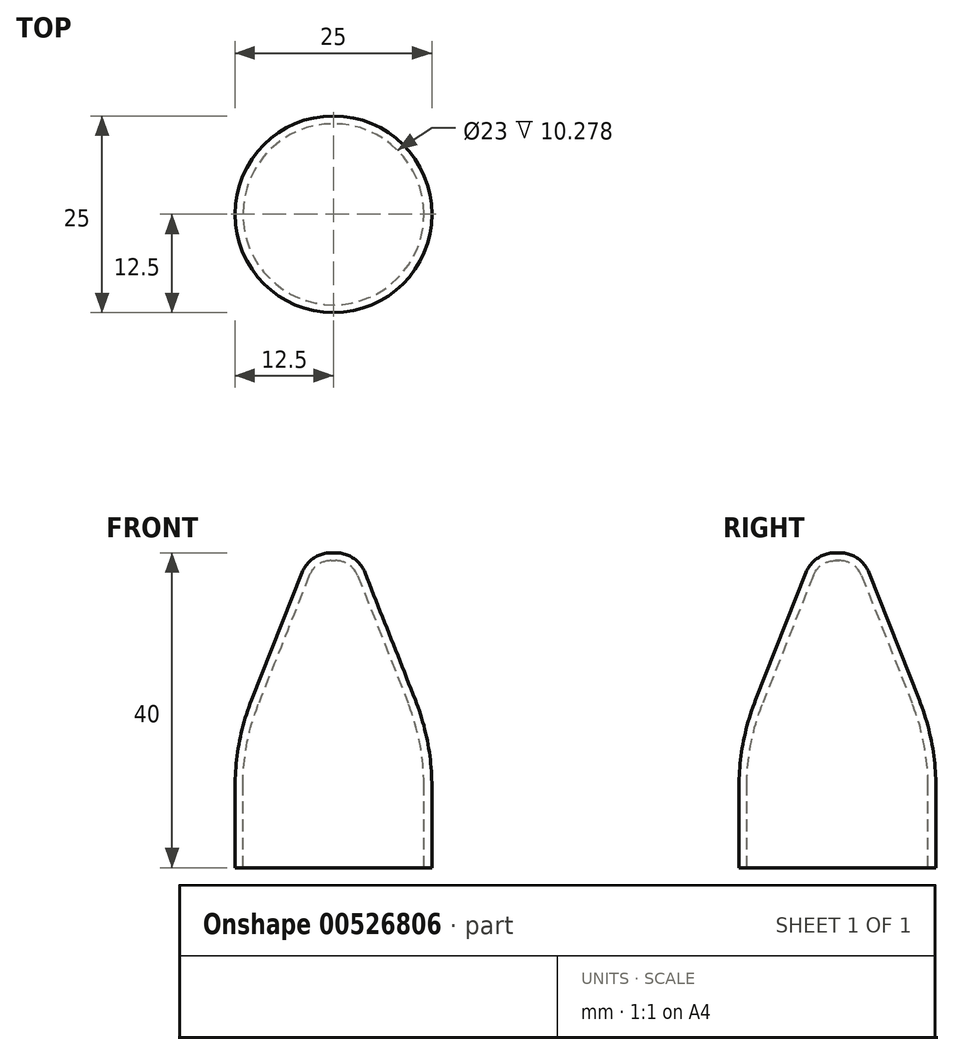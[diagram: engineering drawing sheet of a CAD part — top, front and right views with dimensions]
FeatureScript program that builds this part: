
annotation { "Feature Type Name" : "Feature", "Feature Type Description" : "" }
export const myFeature = defineFeature(function(context is Context, id is Id, definition is map)
    precondition{}
    {
        {
            var Q0;
            Q0=qCreatedBy(makeId("Front.planeOp"),FACE);
            var sketch = newSketch(context, id + "F0", { "sketchPlane" : qUnion([Q0])});
            skLineSegment(sketch, "E0.bottom", {"start": v(0, 0) * mm, "end": v(-12.5, 0) * mm});
            skLineSegment(sketch, "E0.right", {"start": v(-12.5, 0) * mm, "end": v(-12.5, 16) * mm});
            skLineSegment(sketch, "E1", {"start": v(-12.5, 16) * mm, "end": v(-3, 40) * mm});
            skLineSegment(sketch, "E2", {"start": v(-3, 40) * mm, "end": v(0, 40) * mm});
            skLineSegment(sketch, "E3", {"start": v(0, 40) * mm, "end": v(0, 0) * mm});
            skSolve(sketch);
        }
        {
            var Q0;
            Q0=makeQuery(id+"F0.imprint","IMPRINT",FACE,{"disambiguationData":[TD([[makeQuery(id+"F0.imprint","IMPRINT",EDGE,{"derivedFrom":sQuery(id+"F0.wireOp",EDGE,"E0.bottom")}),-1.0]])]});
            var Q1;
            Q1=sQuery(id+"F0.wireOp",EDGE,"E3");
            revolve(context, id + "F1", {"entities" : qUnion([Q0]), "axis" : qUnion([Q1]), "revolveType" : RevolveType.FULL});
        }
        {
            var Q0;
            Q0=makeQuery(id+"F1.opRevolve","SWEPT_EDGE",EDGE,{"disambiguationData":[OSD([sQuery(id+"F0.wireOp",EDGE,"E1"),sQuery(id+"F0.wireOp",EDGE,"E2")])]});
            fillet(context, id + "F2", {"entities" : qUnion([Q0]), "radius" : 4 * mm, "tangentPropagation" : true, "allowEdgeOverflow" : false});
        }
        {
            var Q0;
            Q0=makeQuery(id+"F1.opRevolve","SWEPT_EDGE",EDGE,{"disambiguationData":[OSD([sQuery(id+"F0.wireOp",EDGE,"E0.right"),sQuery(id+"F0.wireOp",EDGE,"E1")])]});
            fillet(context, id + "F3", {"entities" : qUnion([Q0]), "radius" : 30 * mm, "tangentPropagation" : true, "allowEdgeOverflow" : false});
        }
        {
            var Q0;
            Q0=makeQuery(id+"F1.opRevolve","SWEPT_FACE",FACE,{"disambiguationData":[OSD([sQuery(id+"F0.wireOp",EDGE,"E0.bottom")])]});
            shell(context, id + "F4", {"entities" : qUnion([Q0]), "thickness" : 1 * mm});
        }
    });
